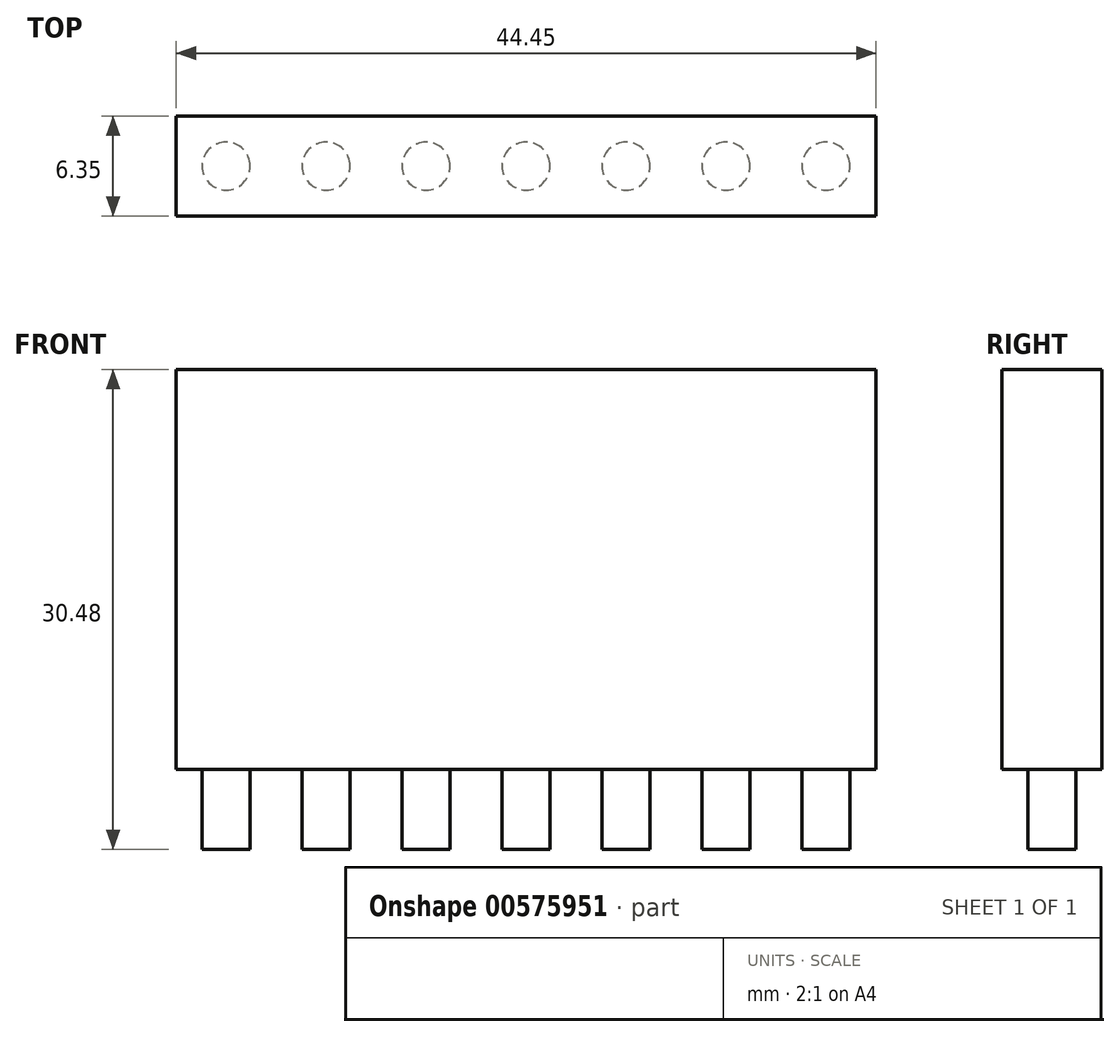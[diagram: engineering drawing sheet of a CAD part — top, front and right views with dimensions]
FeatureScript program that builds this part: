
annotation { "Feature Type Name" : "Feature", "Feature Type Description" : "" }
export const myFeature = defineFeature(function(context is Context, id is Id, definition is map)
    precondition{}
    {
        {
            var Q0;
            Q0=qCreatedBy(makeId("Front.planeOp"),FACE);
            var sketch = newSketch(context, id + "F0", { "sketchPlane" : qUnion([Q0])});
            skLineSegment(sketch, "E0.bottom", {"start": v(25.4, -12.7) * mm, "end": v(-25.4, -12.7) * mm});
            skLineSegment(sketch, "E0.top", {"start": v(25.4, 12.7) * mm, "end": v(-25.4, 12.7) * mm});
            skLineSegment(sketch, "E0.left", {"start": v(25.4, -12.7) * mm, "end": v(25.4, 12.7) * mm});
            skLineSegment(sketch, "E0.right", {"start": v(-25.4, -12.7) * mm, "end": v(-25.4, 12.7) * mm});
            skPoint(sketch, "E0.middle", {"position": v(0, 0) * mm});
            skSolve(sketch);
        }
        {
            var Q0;
            Q0=qSketchRegion(id+"F0",true);
            extrude(context, id + "F1", {"entities" : qUnion([Q0]), "depth" : 6.35 * mm, "offsetDistance" : 25.4 * mm});
        }
        {
            var Q0;
            Q0=makeQuery(id+"F1.opExtrude","SWEPT_FACE",FACE,{"disambiguationData":[OSD([sQuery(id+"F0.wireOp",EDGE,"E0.bottom")])]});
            var sketch = newSketch(context, id + "F2", { "sketchPlane" : qUnion([Q0])});
            skLineSegment(sketch, "E1", {"start": v(-25.4, 3.18) * mm, "end": v(-22.23, 3.18) * mm});
            skPoint(sketch, "E1.endSnap0", {"position": v(-25.4, 3.18) * mm});
            skCircle(sketch, "E2", {"center": v(-22.23, 3.18) * mm, "radius": 1.52 * mm});
            skCircle(sketch, "E3.1.0.0", {"center": v(-15.88, 3.18) * mm, "radius": 1.52 * mm});
            skCircle(sketch, "E3.2.0.0", {"center": v(-9.53, 3.18) * mm, "radius": 1.52 * mm});
            skCircle(sketch, "E3.3.0.0", {"center": v(-3.18, 3.18) * mm, "radius": 1.52 * mm});
            skCircle(sketch, "E3.4.0.0", {"center": v(3.18, 3.18) * mm, "radius": 1.52 * mm});
            skCircle(sketch, "E3.5.0.0", {"center": v(9.53, 3.18) * mm, "radius": 1.52 * mm});
            skCircle(sketch, "E3.6.0.0", {"center": v(15.88, 3.18) * mm, "radius": 1.52 * mm});
            skCircle(sketch, "E3.7.0.0", {"center": v(22.23, 3.18) * mm, "radius": 1.52 * mm});
            skLineSegment(sketch, "E3.direction1", {"start": v(-22.23, 3.18) * mm, "end": v(-15.88, 3.18) * mm, "construction": true});
            skSolve(sketch);
        }
        {
            var Q0;
            Q0=qSketchRegion(id+"F2",true);
            extrude(context, id + "F3", {"entities" : qUnion([Q0]), "operationType" : NewBodyOperationType.ADD, "depth" : 5.08 * mm, "offsetDistance" : 25.4 * mm});
        }
        {
            var Q0;
            Q0=makeQuery(id+"F1.opExtrude","CAP_FACE",FACE,{"disambiguationData":[OSD([sQuery(id+"F0.wireOp",EDGE,"E0.bottom"),sQuery(id+"F0.wireOp",EDGE,"E0.top"),sQuery(id+"F0.wireOp",EDGE,"E0.left"),sQuery(id+"F0.wireOp",EDGE,"E0.right")])],"isStart":false});
            var sketch = newSketch(context, id + "F4", { "sketchPlane" : qUnion([Q0])});
            skLineSegment(sketch, "E4.bottom", {"start": v(25.4, 12.7) * mm, "end": v(19.05, 12.7) * mm});
            skLineSegment(sketch, "E4.top", {"start": v(25.4, -48.54) * mm, "end": v(19.05, -48.54) * mm});
            skLineSegment(sketch, "E4.left", {"start": v(25.4, 12.7) * mm, "end": v(25.4, -48.54) * mm});
            skLineSegment(sketch, "E4.right", {"start": v(19.05, 12.7) * mm, "end": v(19.05, -48.54) * mm});
            skSolve(sketch);
        }
        {
            var Q0;
            Q0 = qSketchRegion(id + "F4", true);
            extrude(context, id + "F5", {"entities" : qUnion([Q0]), "operationType" : NewBodyOperationType.REMOVE, "oppositeDirection" : true, "depth" : 25.4 * mm, "offsetDistance" : 25.4 * mm});
        }
    });
